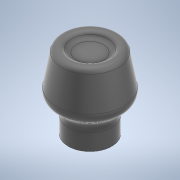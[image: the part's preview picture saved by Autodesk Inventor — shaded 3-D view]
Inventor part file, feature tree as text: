
AUTODESK INVENTOR PART (.ipt)
format: ipt  version: 2020 (Build 240168000, 168)  size: 375,808 bytes
history: native  units: mm
features: sketch x3, extrude x2, revolve x1, fillet x1
ambient origin geometry x8: Origin, YZ Plane, XZ Plane, XY Plane, X Axis, Y Axis, Z Axis, Center Point
bodies: Volumenkörper1 (feature_tree)
feature tree (7):
  sketch  "Skizze2"  dims[d3=13.962634mm d4=4.0mm d5=13.0mm]
  revolve  "Umdrehung1"
  extrude  "Extrusion1"  Depth=1.3mm
  extrude  "Extrusion2"  Depth=4.0mm
  fillet  "Rundung1"  Radius=13.0mm
  sketch  "Skizze1"  dims[d0=1.3mm d1=0.55mm]
  sketch  "Skizze3"  dims[d7=3.0mm d8=1.0mm d9=3.0mm d10=0.0mm d11=90.0deg d12=6.0mm d13=0.0mm d14=3.0mm d15=1.0mm d16=0.0mm d17=2.0mm]
